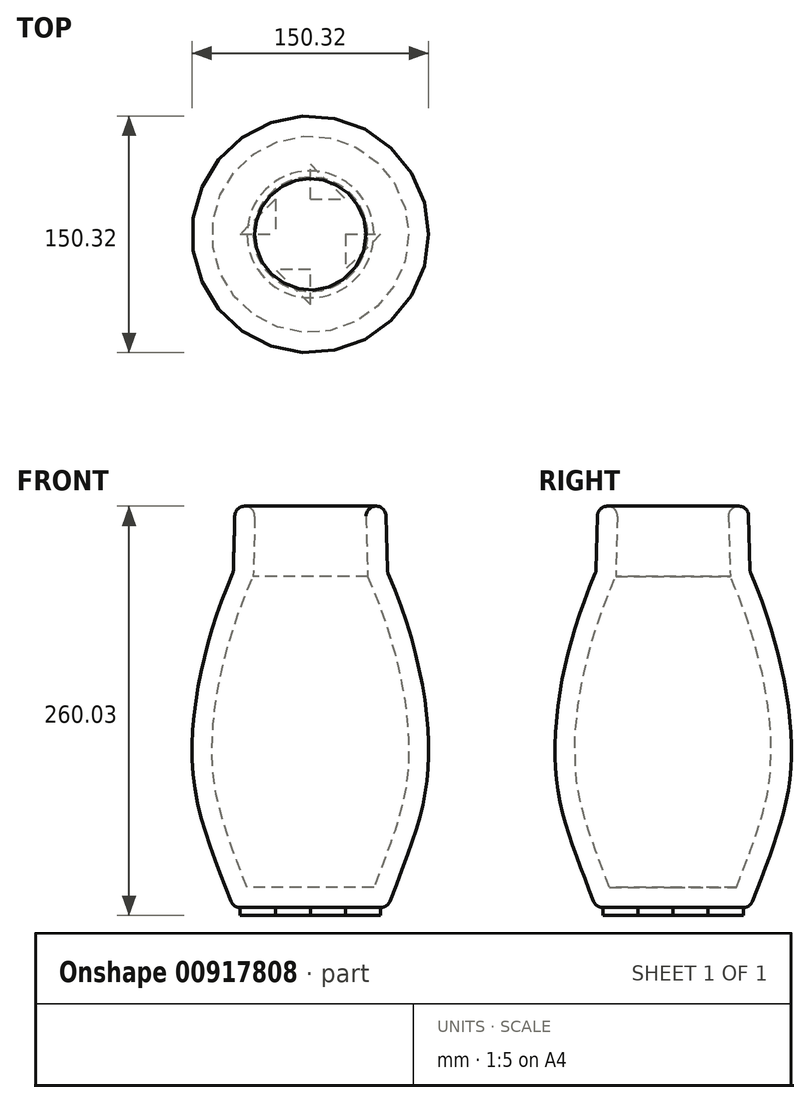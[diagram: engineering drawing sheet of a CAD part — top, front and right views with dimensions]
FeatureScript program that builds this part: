
annotation { "Feature Type Name" : "Feature", "Feature Type Description" : "" }
export const myFeature = defineFeature(function(context is Context, id is Id, definition is map)
    precondition{}
    {
        {
            var Q0;
            Q0=qCreatedBy(makeId("Front.planeOp"),FACE);
            var sketch = newSketch(context, id + "F0", { "sketchPlane" : qUnion([Q0])});
            skLineSegment(sketch, "E0", {"start": v(0, 41.78) * mm, "end": v(47.88, 41.78) * mm});
            skLineSegment(sketch, "E1", {"start": v(48.96, 0) * mm, "end": v(47.88, 41.78) * mm});
            skFitSpline(sketch, "E2", {"points": [v(48.96, 0) * mm, v(75.06, -119.24) * mm, v(48.96, -213.17) * mm], "startDerivative": vector(104.22, -239.9) * mm, "endDerivative": vector(-102.31, -263.88) * mm});
            skLineSegment(sketch, "E3", {"start": v(48.96, -213.17) * mm, "end": v(0, -213.17) * mm});
            skLineSegment(sketch, "E4", {"start": v(0, 41.78) * mm, "end": v(0, -213.17) * mm});
            skSolve(sketch);
        }
        {
            var Q0;
            Q0=makeQuery(id+"F0.imprint","IMPRINT",FACE,{"disambiguationData":[TD([[makeQuery(id+"F0.imprint","IMPRINT",EDGE,{"derivedFrom":sQuery(id+"F0.wireOp",EDGE,"E0")}),-1.0]])]});
            var Q1;
            Q1=sQuery(id+"F0.wireOp",EDGE,"E4");
            revolve(context, id + "F1", {"surfaceOperationType" : NewSurfaceOperationType.NEW, "entities" : qUnion([Q0]), "axis" : qUnion([Q1]), "revolveType" : RevolveType.FULL});
        }
        {
            var Q0;
            Q0=makeQuery(id+"F1.opRevolve","SWEPT_FACE",FACE,{"disambiguationData":[OSD([sQuery(id+"F0.wireOp",EDGE,"E0")])]});
            shell(context, id + "F2", {"entities" : qUnion([Q0]), "thickness" : 12.7 * mm});
        }
        {
            var Q0;
            Q0=makeQuery(id+"F1.opRevolve","SWEPT_EDGE",EDGE,{"disambiguationData":[OSD([sQuery(id+"F0.wireOp",EDGE,"E1"),sQuery(id+"F0.wireOp",EDGE,"E2")])]});
            var Q1;
            Q1=makeQuery(id+"F2.opShell","OFFSET_EDGE",EDGE,{"disambiguationData":[OSD([sQuery(id+"F0.wireOp",EDGE,"E0"),sQuery(id+"F0.wireOp",EDGE,"E1")])]});
            var Q2;
            Q2=makeQuery(id+"F1.opRevolve","SWEPT_EDGE",EDGE,{"disambiguationData":[OSD([sQuery(id+"F0.wireOp",EDGE,"E0"),sQuery(id+"F0.wireOp",EDGE,"E1")])]});
            var Q3;
            Q3=makeQuery(id+"F1.opRevolve","SWEPT_EDGE",EDGE,{"disambiguationData":[OSD([sQuery(id+"F0.wireOp",EDGE,"E2"),sQuery(id+"F0.wireOp",EDGE,"E3")])]});
            fillet(context, id + "F3", {"entities" : qUnion([Q0, Q1, Q2, Q3]), "radius" : 6.35 * mm, "tangentPropagation" : true, "allowEdgeOverflow" : false});
        }
        {
            var Q0;
            Q0=makeQuery(id+"F1.opRevolve","SWEPT_FACE",FACE,{"disambiguationData":[OSD([sQuery(id+"F0.wireOp",EDGE,"E3")])]});
            var sketch = newSketch(context, id + "F4", { "sketchPlane" : qUnion([Q0])});
            skLineSegment(sketch, "E5", {"start": v(0, 44.61) * mm, "end": v(0, -44.61) * mm});
            skLineSegment(sketch, "E6", {"start": v(0, -44.61) * mm, "end": v(-44.61, 0) * mm});
            skLineSegment(sketch, "E7", {"start": v(-44.61, 0) * mm, "end": v(44.61, 0) * mm});
            skLineSegment(sketch, "E8", {"start": v(44.61, 0) * mm, "end": v(0, 44.61) * mm});
            skLineSegment(sketch, "E9", {"start": v(0, 44.61) * mm, "end": v(-44.61, 0) * mm});
            skLineSegment(sketch, "E10", {"start": v(0, -44.61) * mm, "end": v(44.61, 0) * mm});
            skLineSegment(sketch, "E11", {"start": v(-22.3, 22.3) * mm, "end": v(22.3, -22.3) * mm});
            skLineSegment(sketch, "E12", {"start": v(22.3, -22.3) * mm, "end": v(22.3, 22.3) * mm});
            skLineSegment(sketch, "E13", {"start": v(22.3, 22.3) * mm, "end": v(-22.3, -22.3) * mm});
            skLineSegment(sketch, "E14", {"start": v(-22.3, -22.3) * mm, "end": v(-22.3, 22.3) * mm});
            skLineSegment(sketch, "E15", {"start": v(22.3, 22.3) * mm, "end": v(-22.3, 22.3) * mm});
            skLineSegment(sketch, "E16", {"start": v(-22.3, -22.3) * mm, "end": v(22.3, -22.3) * mm});
            skSolve(sketch);
        }
        {
            var Q0;
            {var subQ1=sQuery(id+"F4.wireOp",EDGE,"E5");var subQ4=sQuery(id+"F4.wireOp",EDGE,"E16");var subQ5=makeQuery(id+"F4.imprint","INTERSECT",VERTEX,{"derivedFrom":[subQ1,subQ4]});Q0=makeQuery(id+"F4.imprint","IMPRINT",FACE,{"disambiguationData":[TD([[makeQuery(id+"F4.imprint","IMPRINT",EDGE,{"disambiguationData":[TD([[subQ5,-1.0]])],"derivedFrom":subQ4}),-1.0]])]});}
            var Q1;
            {var subQ0=sQuery(id+"F4.wireOp",EDGE,"E7");var subQ4=sQuery(id+"F4.wireOp",EDGE,"E14");var subQ6=makeQuery(id+"F4.imprint","INTERSECT",VERTEX,{"derivedFrom":[subQ0,subQ4]});Q1=makeQuery(id+"F4.imprint","IMPRINT",FACE,{"disambiguationData":[TD([[makeQuery(id+"F4.imprint","IMPRINT",EDGE,{"disambiguationData":[TD([[subQ6,1.0]])],"derivedFrom":subQ4}),1.0]])]});}
            var Q2;
            {var subQ1=sQuery(id+"F4.wireOp",EDGE,"E5");var subQ4=sQuery(id+"F4.wireOp",EDGE,"E15");var subQ5=makeQuery(id+"F4.imprint","INTERSECT",VERTEX,{"derivedFrom":[subQ1,subQ4]});Q2=makeQuery(id+"F4.imprint","IMPRINT",FACE,{"disambiguationData":[TD([[makeQuery(id+"F4.imprint","IMPRINT",EDGE,{"disambiguationData":[TD([[subQ5,-1.0]])],"derivedFrom":subQ4}),-1.0]])]});}
            var Q3;
            {var subQ1=sQuery(id+"F4.wireOp",EDGE,"E7");var subQ4=sQuery(id+"F4.wireOp",EDGE,"E12");var subQ5=makeQuery(id+"F4.imprint","INTERSECT",VERTEX,{"derivedFrom":[subQ1,subQ4]});Q3=makeQuery(id+"F4.imprint","IMPRINT",FACE,{"disambiguationData":[TD([[makeQuery(id+"F4.imprint","IMPRINT",EDGE,{"disambiguationData":[TD([[subQ5,-1.0]])],"derivedFrom":subQ4}),-1.0]])]});}
            extrude(context, id + "F5", {"entities" : qUnion([Q0, Q1, Q2, Q3]), "operationType" : NewBodyOperationType.ADD, "depth" : 5.08 * mm, "offsetDistance" : 25.4 * mm});
        }
        {
            var Q0;
            Q0=makeQuery(id+"F5.opExtrude","CAP_FACE",FACE,{"disambiguationData":[OSD([sQuery(id+"F4.wireOp",EDGE,"E5"),sQuery(id+"F4.wireOp",EDGE,"E9"),sQuery(id+"F4.wireOp",EDGE,"E15")])],"isStart":false});
            cPlane(context, id + "F6", {"entities" : qUnion([Q0]), "cplaneType" : CPlaneType.OFFSET, "offset" : 0 * mm, "width" : 152.4 * mm, "height" : 152.4 * mm});
        }
    });
